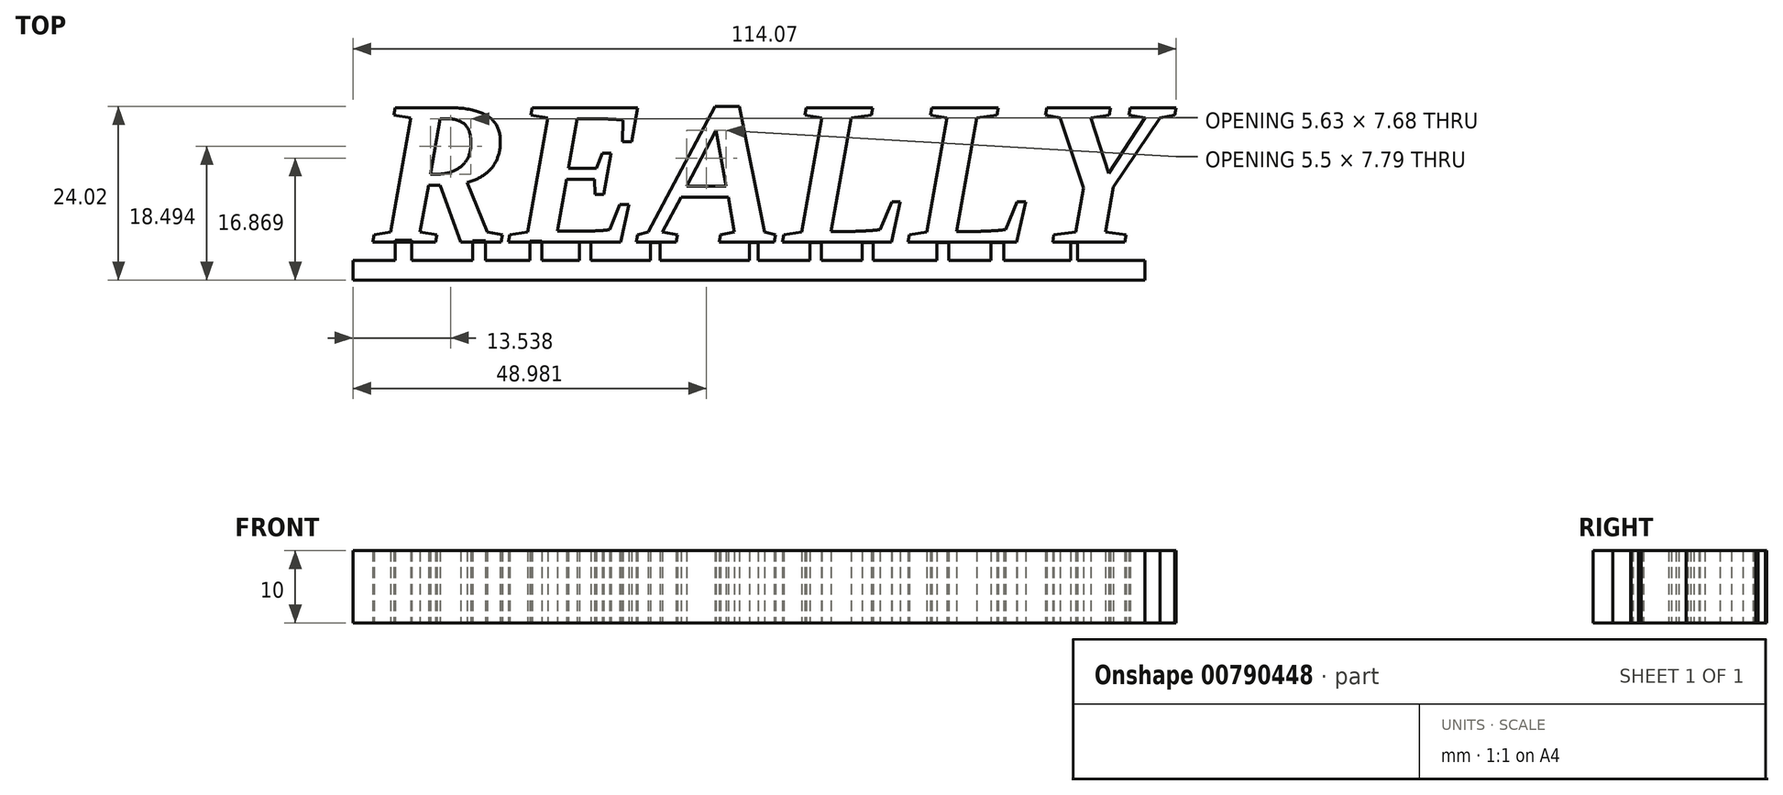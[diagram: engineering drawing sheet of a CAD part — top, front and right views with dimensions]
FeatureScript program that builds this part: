
annotation { "Feature Type Name" : "Feature", "Feature Type Description" : "" }
export const myFeature = defineFeature(function(context is Context, id is Id, definition is map)
    precondition{}
    {
        {
            var Q0;
            Q0=qCreatedBy(makeId("Top.planeOp"),FACE);
            var sketch = newSketch(context, id + "F0", { "sketchPlane" : qUnion([Q0])});
            skText(sketch, "E0", { "text": "REALLY", "fontName": "Tinos-BoldItalic.ttf"});
            const initialGuessF0  = {"E0": [-0.05214, 0.00656, 1, 0, 0.02049]};
            skSetInitialGuess(sketch, initialGuessF0);
            skSolve(sketch);
        }
        {
            var Q0;
            Q0 = qSketchRegion(id + "F0", true);
            extrude(context, id + "F1", {"entities" : qUnion([Q0]), "depth" : 10 * mm, "offsetDistance" : 25 * mm});
        }
        {
            var Q0;
            Q0=qCreatedBy(makeId("Top.planeOp"),FACE);
            var sketch = newSketch(context, id + "F2", { "sketchPlane" : qUnion([Q0])});
            skLineSegment(sketch, "E1.bottom", {"start": v(-54.93, 4.05) * mm, "end": v(54.78, 4.05) * mm});
            skLineSegment(sketch, "E1.top", {"start": v(-54.93, 1.33) * mm, "end": v(54.78, 1.33) * mm});
            skLineSegment(sketch, "E1.left", {"start": v(-54.93, 4.05) * mm, "end": v(-54.93, 1.33) * mm});
            skLineSegment(sketch, "E1.right", {"start": v(54.78, 4.05) * mm, "end": v(54.78, 1.33) * mm});
            skLineSegment(sketch, "E2.bottom", {"start": v(-49.08, 6.84) * mm, "end": v(-46.8, 6.84) * mm});
            skLineSegment(sketch, "E2.top", {"start": v(-49.08, 4.05) * mm, "end": v(-46.8, 4.05) * mm});
            skLineSegment(sketch, "E2.left", {"start": v(-49.08, 6.84) * mm, "end": v(-49.08, 4.05) * mm});
            skLineSegment(sketch, "E2.right", {"start": v(-46.8, 6.84) * mm, "end": v(-46.8, 4.05) * mm});
            skLineSegment(sketch, "E3.bottom", {"start": v(-38.32, 6.76) * mm, "end": v(-36.54, 6.76) * mm});
            skLineSegment(sketch, "E3.top", {"start": v(-38.32, 4.05) * mm, "end": v(-36.54, 4.05) * mm});
            skLineSegment(sketch, "E3.left", {"start": v(-38.32, 6.76) * mm, "end": v(-38.32, 4.05) * mm});
            skLineSegment(sketch, "E3.right", {"start": v(-36.54, 6.76) * mm, "end": v(-36.54, 4.05) * mm});
            skLineSegment(sketch, "E4.bottom", {"start": v(-30.43, 6.68) * mm, "end": v(-28.73, 6.68) * mm});
            skLineSegment(sketch, "E4.top", {"start": v(-30.43, 4.05) * mm, "end": v(-28.73, 4.05) * mm});
            skLineSegment(sketch, "E4.left", {"start": v(-30.43, 6.68) * mm, "end": v(-30.43, 4.05) * mm});
            skLineSegment(sketch, "E4.right", {"start": v(-28.73, 6.68) * mm, "end": v(-28.73, 4.05) * mm});
            skLineSegment(sketch, "E5.bottom", {"start": v(-23.56, 6.6) * mm, "end": v(-21.95, 6.6) * mm});
            skLineSegment(sketch, "E5.top", {"start": v(-23.56, 4.05) * mm, "end": v(-21.95, 4.05) * mm});
            skLineSegment(sketch, "E5.left", {"start": v(-23.56, 6.6) * mm, "end": v(-23.56, 4.05) * mm});
            skLineSegment(sketch, "E5.right", {"start": v(-21.95, 6.6) * mm, "end": v(-21.95, 4.05) * mm});
            skLineSegment(sketch, "E6.bottom", {"start": v(-13.73, 6.5) * mm, "end": v(-12.37, 6.5) * mm});
            skLineSegment(sketch, "E6.top", {"start": v(-13.73, 4.05) * mm, "end": v(-12.37, 4.05) * mm});
            skLineSegment(sketch, "E6.left", {"start": v(-13.73, 6.5) * mm, "end": v(-13.73, 4.05) * mm});
            skLineSegment(sketch, "E6.right", {"start": v(-12.37, 6.5) * mm, "end": v(-12.37, 4.05) * mm});
            skLineSegment(sketch, "E7.bottom", {"start": v(0, 6.5) * mm, "end": v(1.2, 6.5) * mm});
            skLineSegment(sketch, "E7.top", {"start": v(0, 4.05) * mm, "end": v(1.2, 4.05) * mm});
            skLineSegment(sketch, "E7.left", {"start": v(0, 6.5) * mm, "end": v(0, 4.05) * mm});
            skLineSegment(sketch, "E7.right", {"start": v(1.2, 6.5) * mm, "end": v(1.2, 4.05) * mm});
            skLineSegment(sketch, "E8.bottom", {"start": v(8.4, 6.5) * mm, "end": v(10.01, 6.5) * mm});
            skLineSegment(sketch, "E8.top", {"start": v(8.4, 4.05) * mm, "end": v(10.01, 4.05) * mm});
            skLineSegment(sketch, "E8.left", {"start": v(8.4, 6.5) * mm, "end": v(8.4, 4.05) * mm});
            skLineSegment(sketch, "E8.right", {"start": v(10.01, 6.5) * mm, "end": v(10.01, 4.05) * mm});
            skLineSegment(sketch, "E9.bottom", {"start": v(15.61, 6.5) * mm, "end": v(17.14, 6.5) * mm});
            skLineSegment(sketch, "E9.top", {"start": v(15.61, 4.05) * mm, "end": v(17.14, 4.05) * mm});
            skLineSegment(sketch, "E9.left", {"start": v(15.61, 6.5) * mm, "end": v(15.61, 4.05) * mm});
            skLineSegment(sketch, "E9.right", {"start": v(17.14, 6.5) * mm, "end": v(17.14, 4.05) * mm});
            skLineSegment(sketch, "E10.bottom", {"start": v(25.95, 6.5) * mm, "end": v(27.65, 6.5) * mm});
            skLineSegment(sketch, "E10.top", {"start": v(25.95, 4.05) * mm, "end": v(27.65, 4.05) * mm});
            skLineSegment(sketch, "E10.left", {"start": v(25.95, 6.5) * mm, "end": v(25.95, 4.05) * mm});
            skLineSegment(sketch, "E10.right", {"start": v(27.65, 6.5) * mm, "end": v(27.65, 4.05) * mm});
            skLineSegment(sketch, "E11.bottom", {"start": v(33.5, 6.5) * mm, "end": v(35.28, 6.5) * mm});
            skLineSegment(sketch, "E11.top", {"start": v(33.5, 4.05) * mm, "end": v(35.28, 4.05) * mm});
            skLineSegment(sketch, "E11.left", {"start": v(33.5, 6.5) * mm, "end": v(33.5, 4.05) * mm});
            skLineSegment(sketch, "E11.right", {"start": v(35.28, 6.5) * mm, "end": v(35.28, 4.05) * mm});
            skLineSegment(sketch, "E12.bottom", {"start": v(44.52, 6.5) * mm, "end": v(45.46, 6.5) * mm});
            skLineSegment(sketch, "E12.top", {"start": v(44.52, 4.05) * mm, "end": v(45.46, 4.05) * mm});
            skLineSegment(sketch, "E12.left", {"start": v(44.52, 6.5) * mm, "end": v(44.52, 4.05) * mm});
            skLineSegment(sketch, "E12.right", {"start": v(45.46, 6.5) * mm, "end": v(45.46, 4.05) * mm});
            skSolve(sketch);
        }
        {
            var Q0;
            Q0 = qSketchRegion(id + "F2", true);
            extrude(context, id + "F3", {"entities" : qUnion([Q0]), "depth" : 10 * mm, "offsetDistance" : 25 * mm});
        }
    });
